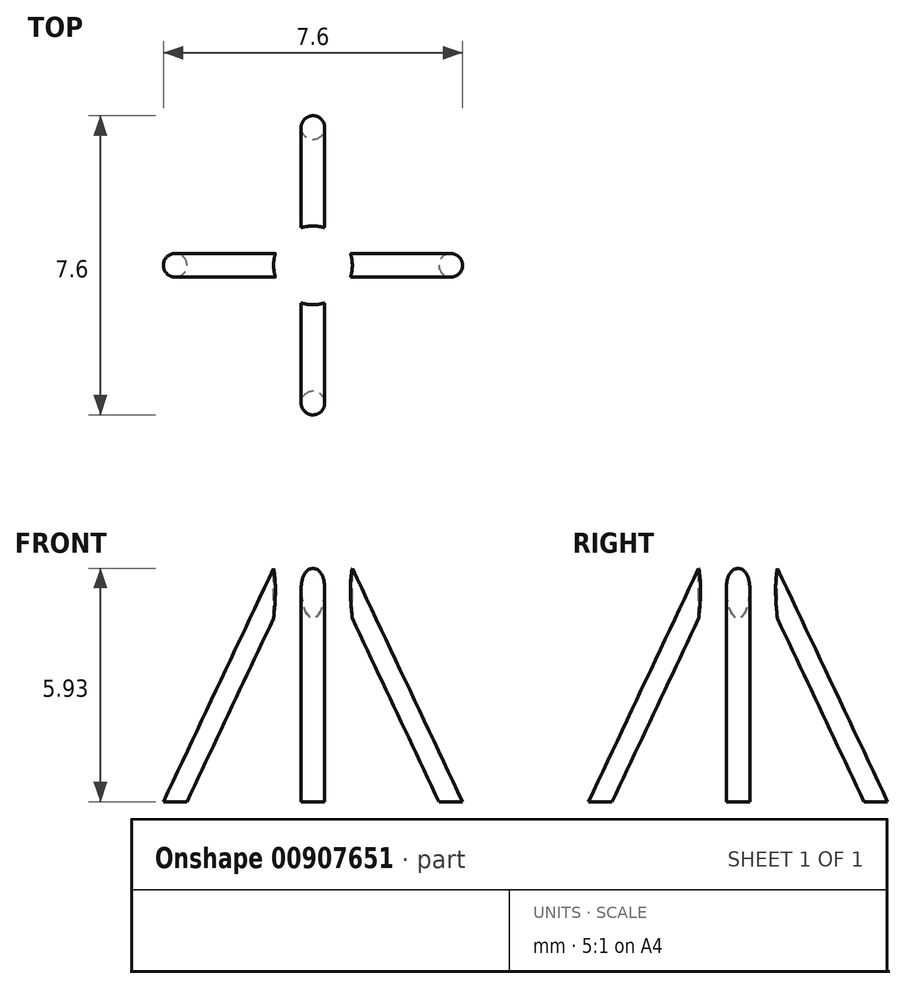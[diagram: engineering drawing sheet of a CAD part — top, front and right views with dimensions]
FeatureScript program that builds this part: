
annotation { "Feature Type Name" : "Feature", "Feature Type Description" : "" }
export const myFeature = defineFeature(function(context is Context, id is Id, definition is map)
    precondition{}
    {
        {
            var Q0;
            Q0=qCreatedBy(makeId("Front.planeOp"),FACE);
            var sketch = newSketch(context, id + "F0", { "sketchPlane" : qUnion([Q0])});
            skLineSegment(sketch, "E0", {"start": v(-1, 6) * mm, "end": v(-1, 0) * mm});
            skLineSegment(sketch, "E1", {"start": v(-1, 0) * mm, "end": v(-4.6, 0) * mm});
            skLineSegment(sketch, "E2", {"start": v(-4.6, 0) * mm, "end": v(-1, 6) * mm});
            skLineSegment(sketch, "E3", {"start": v(-1, 6) * mm, "end": v(0, 6) * mm, "construction": true});
            skLineSegment(sketch, "E4", {"start": v(0, 6) * mm, "end": v(0, 0) * mm, "construction": true});
            skLineSegment(sketch, "E5", {"start": v(0, 0) * mm, "end": v(-1, 0) * mm, "construction": true});
            skLineSegment(sketch, "E6", {"start": v(-3.83, 0) * mm, "end": v(-1, 6) * mm});
            skSolve(sketch);
        }
        {
            var Q0;
            Q0=makeQuery(id+"F0.imprint","IMPRINT",FACE,{"disambiguationData":[TD([[makeQuery(id+"F0.imprint","IMPRINT",EDGE,{"derivedFrom":sQuery(id+"F0.wireOp",EDGE,"E0")}),-1.0]])]});
            var Q1;
            {var subQ0=sQuery(id+"F0.wireOp",EDGE,"E2");Q1=makeQuery(id+"F0.imprint","IMPRINT",FACE,{"disambiguationData":[TD([[makeQuery(id+"F0.imprint","IMPRINT",EDGE,{"derivedFrom":subQ0}),-1.0]])]});}
            var Q2;
            Q2=sQuery(id+"F0.wireOp",EDGE,"E4");
            revolve(context, id + "F1", {"surfaceOperationType" : NewSurfaceOperationType.NEW, "entities" : qUnion([Q0, Q1]), "axis" : qUnion([Q2]), "revolveType" : RevolveType.FULL});
        }
        {
            var Q0;
            Q0=makeQuery(id+"F1.opRevolve","SWEPT_FACE",FACE,{"disambiguationData":[OSD([sQuery(id+"F0.wireOp",EDGE,"E1")])]});
            var sketch = newSketch(context, id + "F2", { "sketchPlane" : qUnion([Q0])});
            skCircle(sketch, "E7", {"center": v(-3.5, 0) * mm, "radius": 0.3 * mm});
            skSolve(sketch);
        }
        {
            var Q0;
            Q0=makeQuery(id+"F2.imprint","IMPRINT",FACE,{"disambiguationData":[TD([[makeQuery(id+"F2.imprint","IMPRINT",EDGE,{"derivedFrom":sQuery(id+"F2.wireOp",EDGE,"E7")}),1.0]])]});
            var Q1;
            Q1=sQuery(id+"F0.wireOp",EDGE,"E6");
            sweep(context, id + "F3", {"profiles" : qUnion([Q0]), "path" : qUnion([Q1])});
        }
        {
            var Q0;
            Q0=makeQuery(id+"F3.opSweep","SWEPT_BODY",BODY,{"disambiguationData":[OSD([sQuery(id+"F0.wireOp",EDGE,"E6"),sQuery(id+"F2.wireOp",EDGE,"E7")])]});
            var Q1;
            Q1=makeQuery(id+"F1.opRevolve","SWEPT_EDGE",EDGE,{"disambiguationData":[OSD([sQuery(id+"F0.wireOp",EDGE,"E0"),sQuery(id+"F0.wireOp",EDGE,"E2"),sQuery(id+"F0.wireOp",EDGE,"E6")])]});
            circularPattern(context, id + "F4", {"entities" : qUnion([Q0]), "axis" : qUnion([Q1]), "angle" : 360 * degree, "instanceCount" : 4, "equalSpace" : true});
        }
        {
            var Q0;
            Q0=makeQuery(id+"F3.opSweep","CAP_FACE",FACE,{"disambiguationData":[OSD([sQuery(id+"F0.wireOp",VERTEX,"E6.end"),sQuery(id+"F2.wireOp",EDGE,"E7")])],"isStart":false});
            var sketch = newSketch(context, id + "F5", { "sketchPlane" : qUnion([Q0])});
            skCircle(sketch, "E8", {"center": v(0, 0) * mm, "radius": 1 * mm});
            skSolve(sketch);
        }
        {
            var Q0;
            Q0 = qSketchRegion(id + "F5", true);
            extrude(context, id + "F6", {"entities" : qUnion([Q0]), "operationType" : NewBodyOperationType.REMOVE, "oppositeDirection" : true, "depth" : 6 * mm, "offsetDistance" : 25 * mm});
        }
        {
            var Q0;
            Q0=makeQuery(id+"F1.opRevolve","SWEPT_BODY",BODY,{"disambiguationData":[OSD([sQuery(id+"F0.wireOp",EDGE,"E0"),sQuery(id+"F0.wireOp",EDGE,"E1"),sQuery(id+"F0.wireOp",EDGE,"E2")])]});
            deleteBodies(context, id + "F7", {"entities" : qUnion([Q0])});
        }
    });
